# Revit family: Outdoor-Kitchen-Equipment_Kalamazoo-Smoker-Cabinets1
name_source: partatom
category: Specialty Equipment
revit_build: Autodesk Revit 2018 (Build: 20190510_1515(x64)
units: mm (PartAtom-declared; Revit-internal decimal feet)

## family parameters
Always vertical = Yes
Cut with Voids When Loaded = No
OmniClass Number = 23.40.40.14.17
OmniClass Title = Food Cooking Equipment
Part Type = Normal
Room Calculation Point = No
Round Connector Dimension = Use Diameter
Shared = No
Work Plane-Based = No

## types (2) — shared parameters
Apparent Load = 360 VA
Assembly Code = E1090300
Current = 3 A
Edition number = 1
Frequency = 60 Hz
Keynote = 11400
Manufacturer = Kalamazoo Outdoor Gourmet
Number of Poles = 3
Power Factor = 0.8
Product Guid = 2cceb01d-0b20-4e6c-b607-23c7b917c3ba
Product Material = Kalamazoo - Stainless Steel - 304 OR 316L
Product data url = https://www.bimobject.com
Total Heating Capacity = 0.0 Btu/h
URL = https://kalamazoogourmet.com
Voltage = 120 V
Ι_Gnrc Mdl Optn 01 = Extension : +3/4"
Ι_Gnrc Mdl Optn 02 = Extension : -3/4"

## per-type parameters (varying)
| type | Depth | Description | Weight (lb) | Width | Ι_FT60 | Ι_FT70 |
| K-SMOKE-36 | 30 " | Built-In Smoker Cabinet | 405.00 lbf | 36 " | No | Yes |
| K-SMOKE-42-R | 32.63 " | Freestanding Smoker Cabinet | 490.00 lbf | 48.3 " | Yes | No |

note: column(s) folded — value = type name in every type: Model

## geometry (parser evidence)
native form markers: Sweep x6
no freeform markers — native parametric forms only
